# Revit family: Domotics-DomesticRanges-GEWISS-CHORUS_DATA-SOCKET-OUTLET_PHONE_ENG
name_source: partatom
category: Apparecchi elettrici
revit_build: Autodesk Revit 2016 (Build: 20161004_0715(x64)
units: mm (PartAtom-declared; Revit-internal decimal feet)

## family parameters
Condiviso = Sì
Host = Superficie
Mantenere orientamento annotazione = Sì
Numero OmniClass = 23.80.50.11.14
Punto di calcolo locali = Sì
Quota connettore circolare = Usa diametro
Taglio con vuoti quando caricato = Sì
Tipo di parte = Normale
Titolo OmniClass = Switches

## types (3) — shared parameters
Carico apparente = 0 VA
Catalogue = DOMOTICS
Catalogue Range = CHORUS - DOMESTIC RANGE
Electrocod = 3722
Finitura pulsante = GEWISS ACCIAIO TITANIO
IDF = df9d88d5-13ea-46c3-aa78-49abfe027388
IDT = 877b9bdb-bb23-4ec1-8ae3-ce0bddbed5e2
Immagine tipo = GW14406.jpg
Larghezza pulsante = 23 mm  [stored 0.0754593 ft]
N. poli = 1
Produttore = GEWISS S.p.A.
Prospetto di default = 1219 mm
Technical sheet = https://www.gewiss.com
Tipo_ = SYSTEM PRESE TEL ENG_BASE : GW - Titanio
URL = https://www.gewiss.com
Version file RFA = 19.0
Volt = 230 V

## per-type parameters (varying)
| type | Descrizione | EAN code | Modello |
| GW12406 - TELEPHONE CONNECTOR BRITISH ST BLACK | TELEPHONE CONNECTOR BRITISH ST BLACK | 8011564269088 | GW12406 |
| GW14406 - TELEPHONE CONNECTOR BRITISH ST TITANIUM | TELEPHONE CONNECTOR BRITISH ST TITANIUM | 8011564267237 | GW14406 |
| GW10406 - TELEPHONE CONNECTOR BRITISH ST WHITE | TELEPHONE CONNECTOR BRITISH ST WHITE | 8011564259447 | GW10406 |

note: [stored X ft] marks values corroborated as IEEE doubles in the binary element streams (Revit-internal decimal feet)

## geometry (parser evidence)
native form markers: Sweep x2
no freeform markers — native parametric forms only
